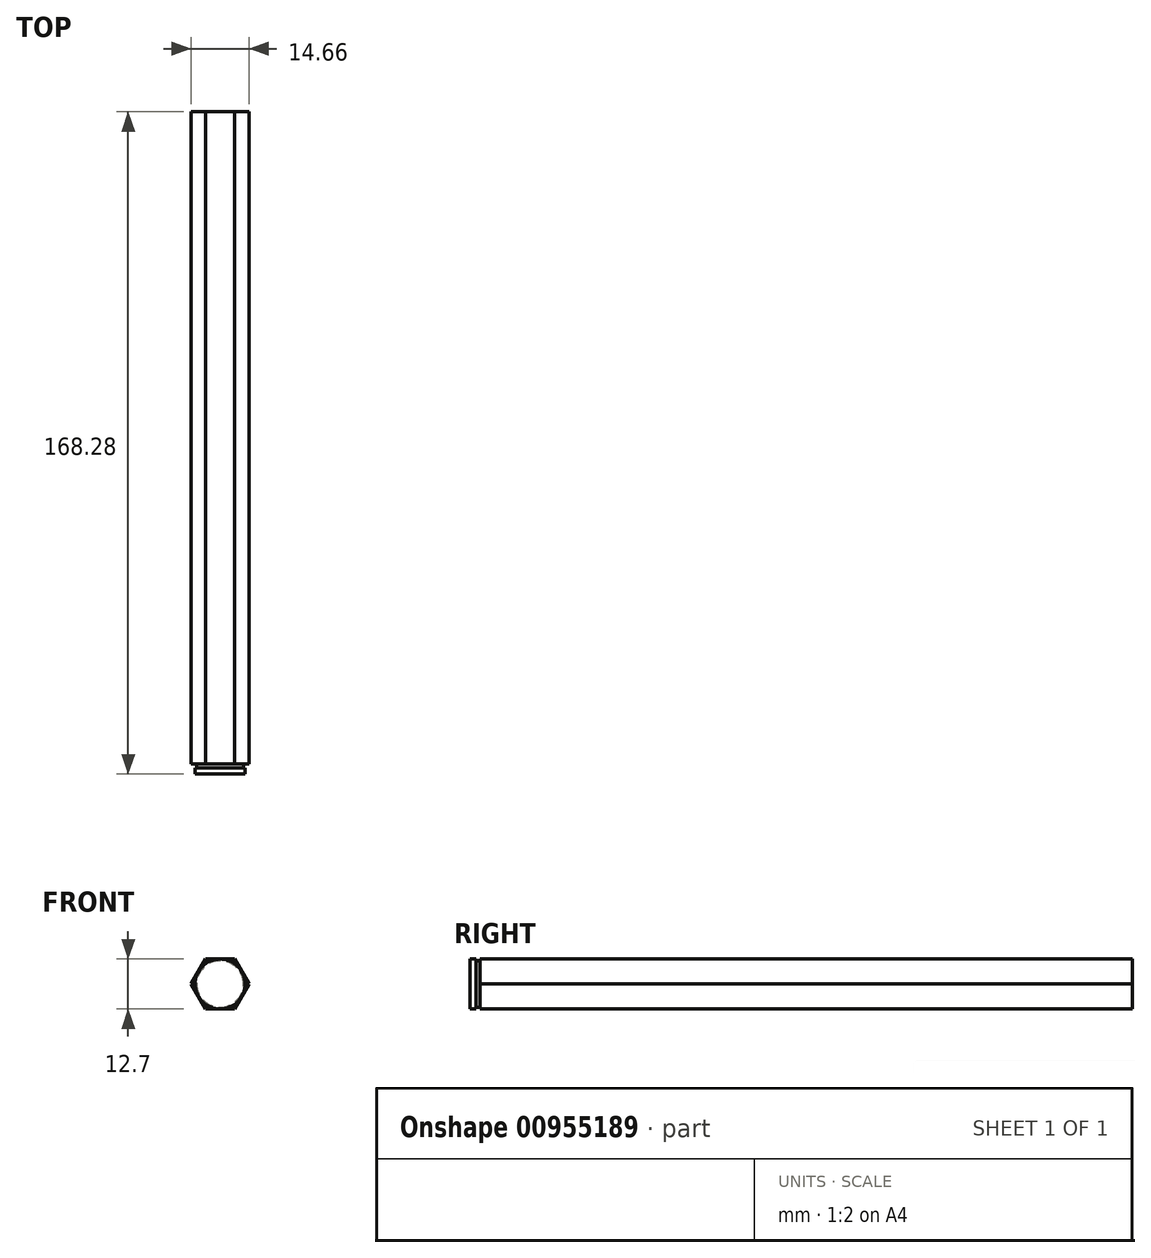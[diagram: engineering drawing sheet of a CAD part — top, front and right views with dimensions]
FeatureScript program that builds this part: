
annotation { "Feature Type Name" : "Feature", "Feature Type Description" : "" }
export const myFeature = defineFeature(function(context is Context, id is Id, definition is map)
    precondition{}
    {
        {
            var Q0;
            Q0=qCreatedBy(makeId("Front.planeOp"),FACE);
            var sketch = newSketch(context, id + "F0", { "sketchPlane" : qUnion([Q0])});
            skCircle(sketch, "E0.cCircle", {"center": v(0, 0) * mm, "radius": 6.35 * mm, "construction": true});
            skLineSegment(sketch, "E0.0", {"start": v(-3.67, 6.35) * mm, "end": v(3.67, 6.35) * mm});
            skLineSegment(sketch, "E0.1", {"start": v(3.67, 6.35) * mm, "end": v(7.33, 0) * mm});
            skLineSegment(sketch, "E0.2", {"start": v(7.33, 0) * mm, "end": v(3.67, -6.35) * mm});
            skLineSegment(sketch, "E0.3", {"start": v(3.67, -6.35) * mm, "end": v(-3.67, -6.35) * mm});
            skLineSegment(sketch, "E0.4", {"start": v(-3.67, -6.35) * mm, "end": v(-7.33, 0) * mm});
            skLineSegment(sketch, "E0.5", {"start": v(-7.33, 0) * mm, "end": v(-3.67, 6.35) * mm});
            skPoint(sketch, "E0.0.midPoint", {"position": v(0, 6.35) * mm});
            skSolve(sketch);
        }
        {
            var Q0;
            Q0=qSketchRegion(id+"F0",true);
            extrude(context, id + "F1", {"entities" : qUnion([Q0]), "depth" : 168.27 * mm, "offsetDistance" : 25.4 * mm});
        }
        {
            var Q0;
            Q0=qCreatedBy(makeId("Top.planeOp"),FACE);
            var sketch = newSketch(context, id + "F2", { "sketchPlane" : qUnion([Q0])});
            skLineSegment(sketch, "E1", {"start": v(-7.33, -165.7) * mm, "end": v(-5.94, -165.7) * mm});
            skLineSegment(sketch, "E2", {"start": v(-5.94, -165.7) * mm, "end": v(-5.94, -166.69) * mm});
            skLineSegment(sketch, "E3", {"start": v(-5.94, -166.69) * mm, "end": v(-6.35, -166.69) * mm});
            skLineSegment(sketch, "E4", {"start": v(-6.35, -166.69) * mm, "end": v(-6.35, -168.28) * mm});
            skLineSegment(sketch, "E5", {"start": v(0, -168.28) * mm, "end": v(0, 0) * mm, "construction": true});
            skLineSegment(sketch, "E6", {"start": v(-7.33, -165.7) * mm, "end": v(-7.33, -168.28) * mm});
            skLineSegment(sketch, "E7", {"start": v(-7.33, -168.28) * mm, "end": v(-6.35, -168.28) * mm});
            skSolve(sketch);
        }
        {
            var Q0;
            Q0=qSketchRegion(id+"F2",true);
            var Q1;
            Q1=sQuery(id+"F2.wireOp",EDGE,"E5");
            revolve(context, id + "F3", {"operationType" : NewBodyOperationType.REMOVE, "surfaceOperationType" : NewSurfaceOperationType.NEW, "entities" : qUnion([Q0]), "axis" : qUnion([Q1]), "revolveType" : RevolveType.FULL, "oppositeDirection" : true});
        }
    });
